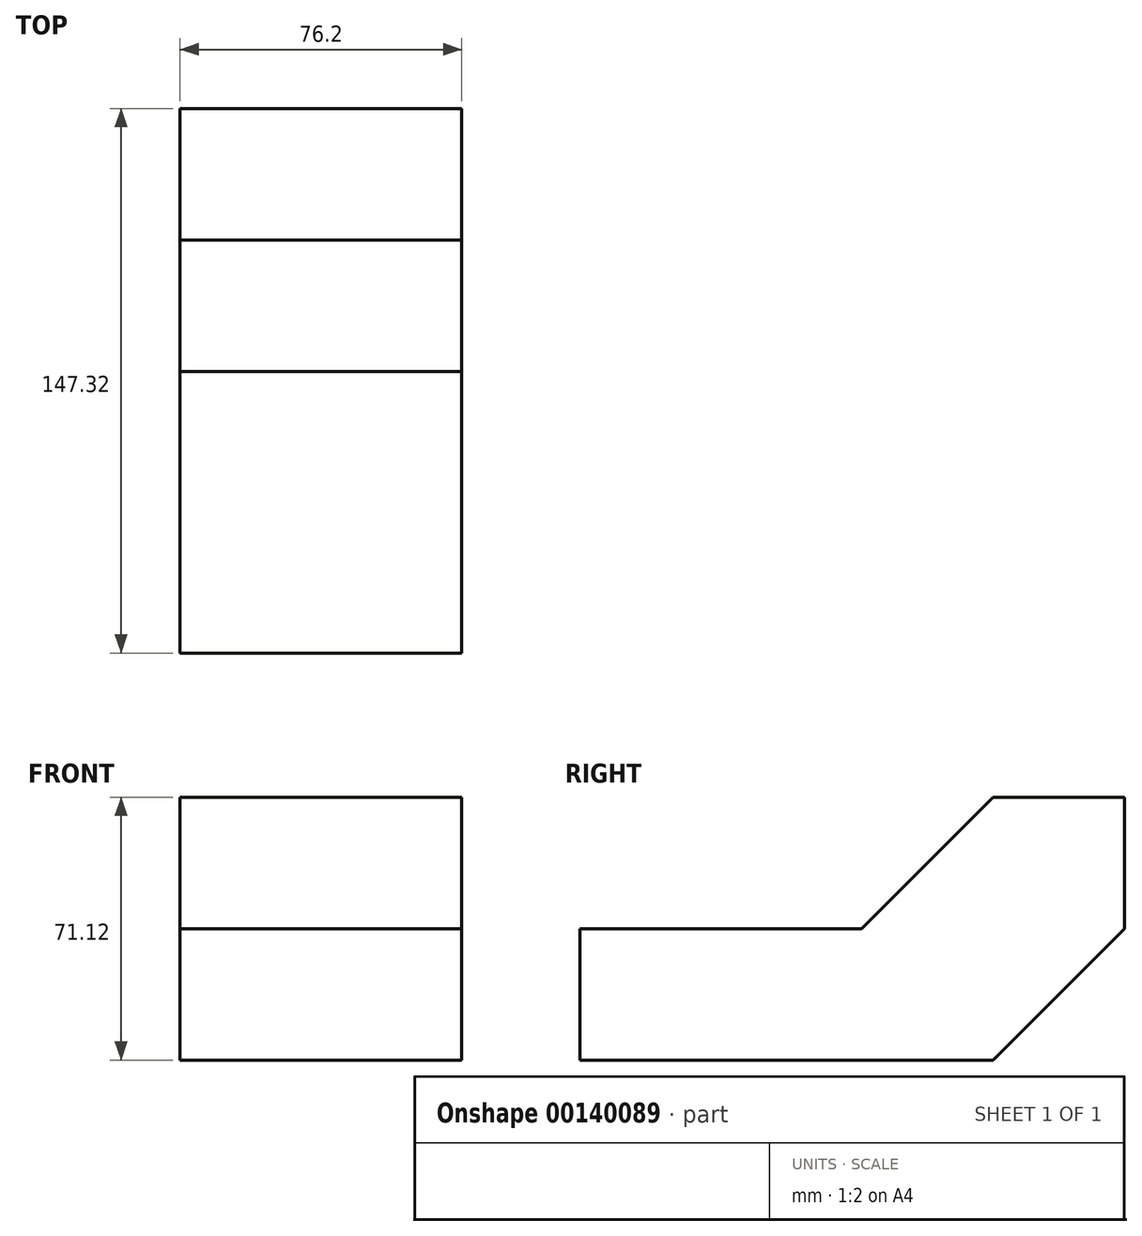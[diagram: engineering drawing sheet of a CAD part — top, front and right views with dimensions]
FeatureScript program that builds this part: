
annotation { "Feature Type Name" : "Feature", "Feature Type Description" : "" }
export const myFeature = defineFeature(function(context is Context, id is Id, definition is map)
    precondition{}
    {
        {
            var Q0;
            Q0=qCreatedBy(makeId("Right.planeOp"),FACE);
            var sketch = newSketch(context, id + "F0", { "sketchPlane" : qUnion([Q0])});
            skLineSegment(sketch, "E0", {"start": v(0, 0) * mm, "end": v(0, 35.56) * mm});
            skLineSegment(sketch, "E1", {"start": v(0, 35.56) * mm, "end": v(76.2, 35.56) * mm});
            skLineSegment(sketch, "E2", {"start": v(76.2, 35.56) * mm, "end": v(76.2, 71.12) * mm});
            skLineSegment(sketch, "E3", {"start": v(76.2, 71.12) * mm, "end": v(147.32, 71.12) * mm});
            skLineSegment(sketch, "E4", {"start": v(147.32, 71.12) * mm, "end": v(147.32, 0) * mm});
            skLineSegment(sketch, "E5", {"start": v(147.32, 0) * mm, "end": v(0, 0) * mm});
            skSolve(sketch);
        }
        {
            var Q0;
            Q0 = qSketchRegion(id + "F0", true);
            extrude(context, id + "F1", {"entities" : qUnion([Q0]), "depth" : 76.2 * mm});
        }
        {
            var Q0;
            Q0=qCreatedBy(makeId("Right.planeOp"),FACE);
            var sketch = newSketch(context, id + "F2", { "sketchPlane" : qUnion([Q0])});
            skLineSegment(sketch, "E6", {"start": v(111.76, 0) * mm, "end": v(147.32, 35.56) * mm});
            skLineSegment(sketch, "E7", {"start": v(147.32, 35.56) * mm, "end": v(147.32, 0) * mm});
            skLineSegment(sketch, "E8", {"start": v(147.32, 0) * mm, "end": v(111.76, 0) * mm});
            skLineSegment(sketch, "E9", {"start": v(76.2, 35.56) * mm, "end": v(111.76, 71.12) * mm});
            skLineSegment(sketch, "E10", {"start": v(111.76, 71.12) * mm, "end": v(76.2, 71.12) * mm});
            skLineSegment(sketch, "E11", {"start": v(76.2, 71.12) * mm, "end": v(76.2, 35.56) * mm});
            skSolve(sketch);
        }
        {
            var Q0;
            Q0 = qSketchRegion(id + "F2", true);
            extrude(context, id + "F3", {"entities" : qUnion([Q0]), "operationType" : NewBodyOperationType.REMOVE, "depth" : 76.2 * mm});
        }
    });
